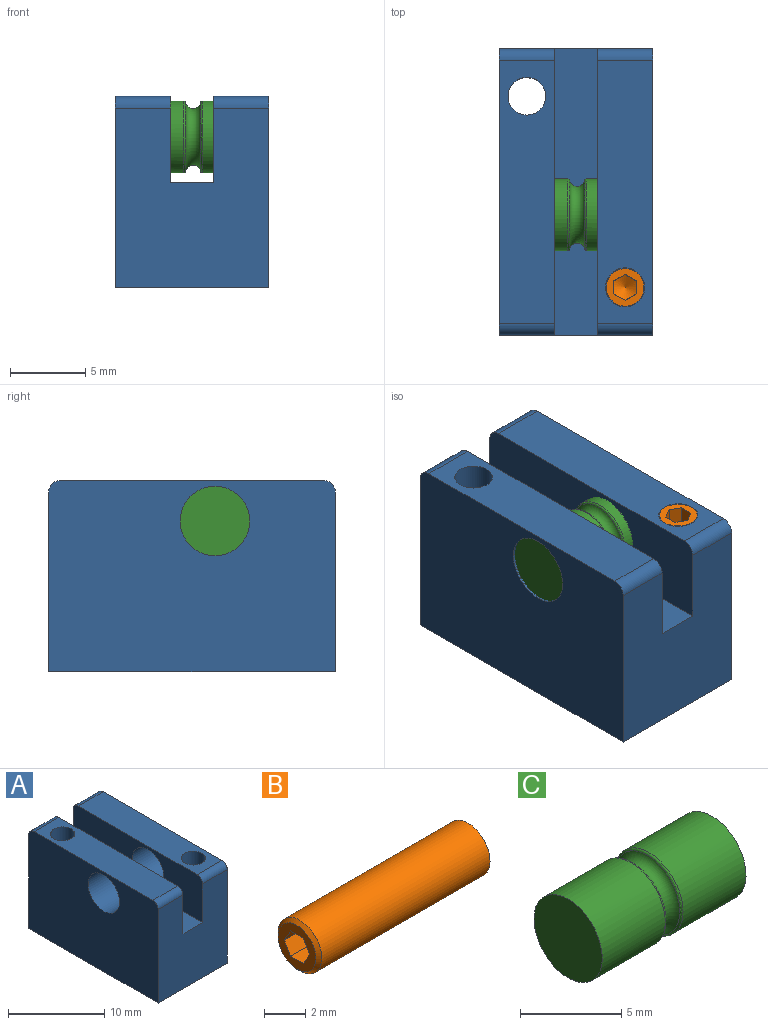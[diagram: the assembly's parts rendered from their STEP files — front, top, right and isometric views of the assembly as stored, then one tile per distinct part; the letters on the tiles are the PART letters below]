
ASSEMBLY  parts=3 mates=2
PART A: 18 faces, bbox 10.2x19.1x12.7 mm
  f0: plane 17.48x3.66mm, normal (0,0,1), area 59mm2, adj f4,f8,f10,f11,f15
  f1: plane 11.91x10.19mm, normal (0,1,0), area 107.2mm2, adj f2,f4,f6,f7,f8,f9,f10,f13
  f2: plane 19.05x12.7mm, normal (-1,0,0), area 224.9mm2, adj f1,f3,f5,f6,f12,f13,f17
  f3: plane 11.91x10.19mm, normal (0,-1,0), area 107.2mm2, adj f2,f4,f6,f7,f8,f9,f11,f12
  f4: plane 19.05x12.7mm, normal (1,0,0), area 224.9mm2, adj f0,f1,f3,f6,f10,f11,f16
  f5: plane 17.48x3.66mm, normal (0,0,1), area 59mm2, adj f2,f7,f12,f13,f14
  f6: plane 19.05x10.19mm, normal (0,0,-1), area 184.2mm2, adj f1,f2,f3,f4,f14,f15
  f7: plane 19.05x5.72mm, normal (1,0,0), area 91.8mm2, adj f1,f3,f5,f9,f12,f13,f17
  f8: plane 19.05x5.72mm, normal (-1,0,0), area 91.8mm2, adj f0,f1,f3,f9,f10,f11,f16
  f9: plane 19.05x2.87mm, normal (0,0,1), area 54.7mm2, adj f1,f3,f7,f8
  f10: cylinder r=0.79mm len=3.66mm, axis (1,0,0), area 4.5mm2, adj f0,f1,f4,f8
  f11: cylinder r=0.79mm len=3.66mm, axis (-1,0,0), area 4.5mm2, adj f0,f3,f4,f8
  f12: cylinder r=0.79mm len=3.66mm, axis (-1,0,0), area 4.5mm2, adj f2,f3,f5,f7
  f13: cylinder r=0.79mm len=3.66mm, axis (1,0,0), area 4.5mm2, adj f1,f2,f5,f7
  f14: cylinder r=1.25mm len=12.7mm, axis (0,0,1), area 99.7mm2, adj f5,f6
  f15: cylinder r=1.25mm len=12.7mm, axis (0,0,1), area 99.7mm2, adj f0,f6
  f16: cylinder r=2.31mm len=4.62mm, axis (1,0,0), area 53.1mm2, adj f4,f8
  f17: cylinder r=2.31mm len=4.62mm, axis (1,0,0), area 53.1mm2, adj f2,f7
PART B: 11 faces, bbox 12.3x3.3x3.3 mm
  f0: cone r=1732.05mm half-angle=60deg, axis (-1,0,0), area 2.6mm2, adj f5,f6,f7,f8,f9,f10
  f1: sphere r=4.2mm, area 7.3mm2, adj f2
  f2: cylinder r=1.5mm len=11.52mm, axis (-1,0,0), area 108.6mm2, adj f1,f3
  f3: cone r=1.3mm half-angle=45deg, axis (1,0,0), area 2.5mm2, adj f2,f4
  f4: plane 2.6x2.6mm, normal (-1,0,0), area 3.4mm2, adj f3,f5,f6,f7,f8,f9,f10
  f5: plane 3.27x1.02mm, normal (0,-0.87,-0.5), area 2.6mm2, adj f0,f4,f6,f10
  f6: plane 3.07x0.94mm, normal (0,0,-1), area 2.6mm2, adj f0,f4,f5,f7
  f7: plane 3.27x1.02mm, normal (0,0.87,-0.5), area 2.6mm2, adj f0,f4,f6,f8
  f8: plane 3.27x1.02mm, normal (0,0.87,0.5), area 2.6mm2, adj f0,f4,f7,f9
  f9: plane 3.07x0.94mm, normal (0,0,1), area 2.6mm2, adj f0,f4,f8,f10
  f10: plane 3.27x1.02mm, normal (0,-0.87,0.5), area 2.6mm2, adj f0,f4,f5,f9
PART C: 7 faces, bbox 10x5.2x5.2 mm
  f0: plane 4.76x4.76mm, normal (-1,0,0), area 17.8mm2, adj f4
  f1: plane 4.76x4.76mm, normal (1,0,0), area 17.8mm2, adj f2
  f2: cylinder r=2.38mm len=4.76mm, axis (-1,0,0), area 65.7mm2, adj f1,f5
  f3: torus R=2.38mm, axis (-1,0,0), area 17.6mm2, adj f5,f6
  f4: cylinder r=2.38mm len=4.76mm, axis (-1,0,0), area 65.7mm2, adj f0,f6
  f5: torus R=2.25mm, axis (1,0,0), area 2.6mm2, adj f2,f3
  f6: torus R=2.25mm, axis (1,0,0), area 2.6mm2, adj f3,f4
PLACE A t=(7.44,9.8,-10.06)mm
PLACE B rot(axis=(0,1,0),90deg) t=(10.96,2.31,2.64)mm
PLACE C t=(2.76,7.13,-0.05)mm
MATE fastened A.f16 <-> C.f2  axis (1,0,0) through (12.79,7.13,-0.05)mm
MATE fastened B.f0 <-> A.f15  axis (0,0,1) through (10.96,2.31,2.64)mm
